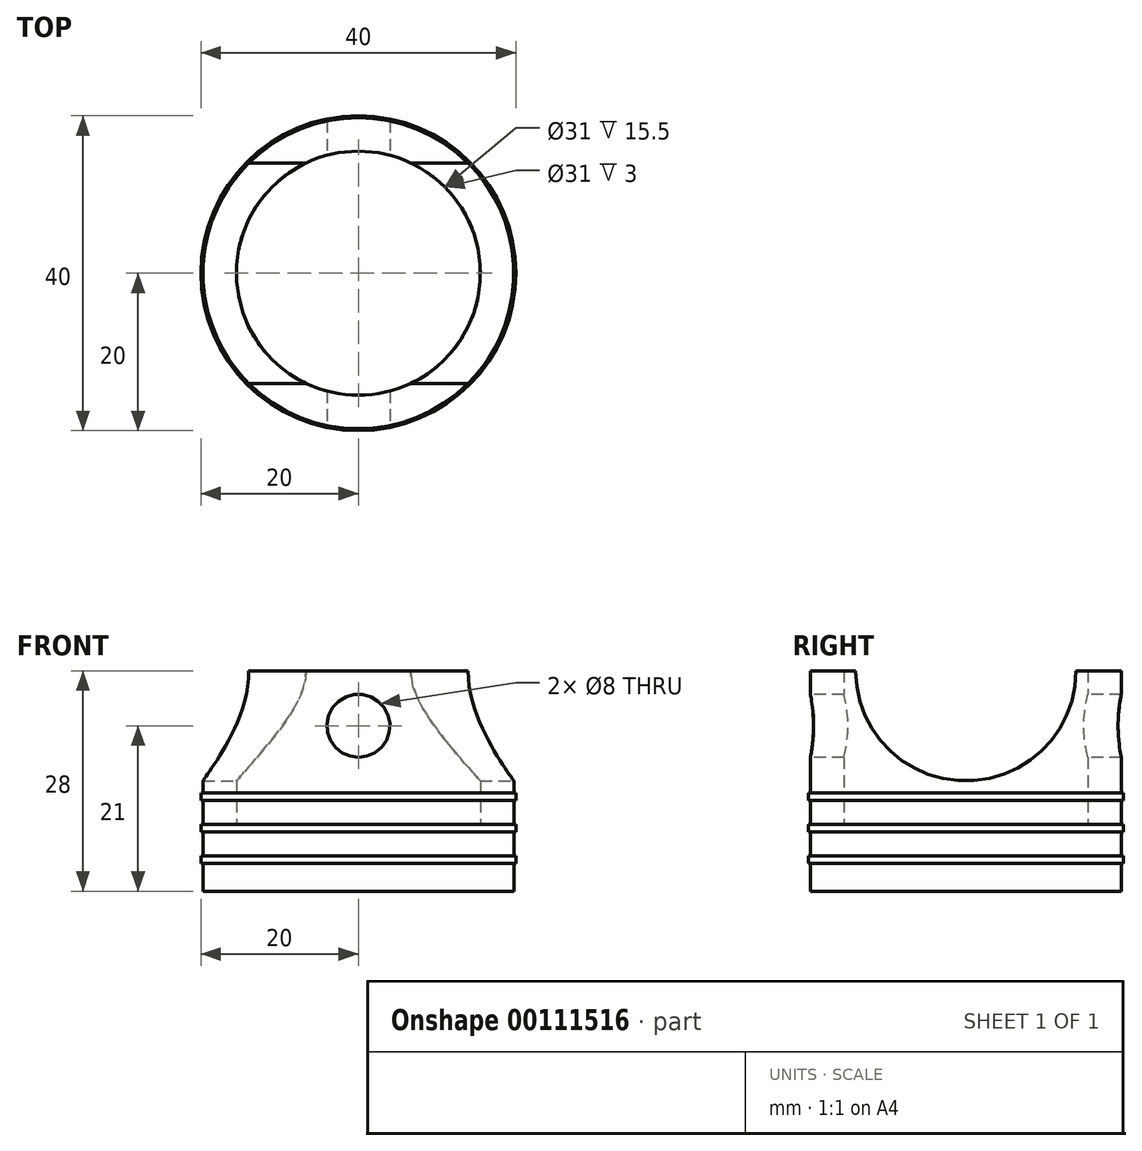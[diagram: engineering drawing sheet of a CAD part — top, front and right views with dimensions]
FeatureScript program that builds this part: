
annotation { "Feature Type Name" : "Feature", "Feature Type Description" : "" }
export const myFeature = defineFeature(function(context is Context, id is Id, definition is map)
    precondition{}
    {
        {
            var Q0;
            Q0=qCreatedBy(makeId("Top.planeOp"),FACE);
            var sketch = newSketch(context, id + "F0", { "sketchPlane" : qUnion([Q0])});
            skCircle(sketch, "E0", {"center": v(0, 0) * mm, "radius": 19.75 * mm});
            skCircle(sketch, "E1", {"center": v(0, 0) * mm, "radius": 15.5 * mm});
            skSolve(sketch);
        }
        {
            var Q0;
            Q0=makeQuery(id+"F0.imprint","IMPRINT",FACE,{"disambiguationData":[TD([[makeQuery(id+"F0.imprint","IMPRINT",EDGE,{"derivedFrom":sQuery(id+"F0.wireOp",EDGE,"E0")}),1.0]])]});
            extrude(context, id + "F1", {"entities" : qUnion([Q0]), "depth" : 28 * mm});
        }
        {
            var Q0;
            Q0=makeQuery(id+"F0.imprint","IMPRINT",FACE,{"disambiguationData":[TD([[makeQuery(id+"F0.imprint","IMPRINT",EDGE,{"derivedFrom":sQuery(id+"F0.wireOp",EDGE,"E1")}),1.0]])]});
            extrude(context, id + "F2", {"entities" : qUnion([Q0]), "operationType" : NewBodyOperationType.ADD, "depth" : 8 * mm});
        }
        {
            var Q0;
            Q0=qCreatedBy(makeId("Front.planeOp"),FACE);
            var sketch = newSketch(context, id + "F3", { "sketchPlane" : qUnion([Q0])});
            skLineSegment(sketch, "E2", {"start": v(0, 0) * mm, "end": v(0, 21) * mm});
            skCircle(sketch, "E3", {"center": v(0, 21) * mm, "radius": 4 * mm});
            skLineSegment(sketch, "E4", {"start": v(0, 21) * mm, "end": v(0, 28) * mm});
            skSolve(sketch);
        }
        {
            var Q0;
            Q0 = qSketchRegion(id + "F3", true);
            extrude(context, id + "F4", {"entities" : qUnion([Q0]), "operationType" : NewBodyOperationType.REMOVE, "endBound" : BoundingType.SYMMETRIC, "oppositeDirection" : true, "depth" : 100 * mm});
        }
        {
            var Q0;
            Q0=qCreatedBy(makeId("Front.planeOp"),FACE);
            var sketch = newSketch(context, id + "F5", { "sketchPlane" : qUnion([Q0])});
            skLineSegment(sketch, "E5", {"start": v(0, 0) * mm, "end": v(0, 4) * mm});
            skLineSegment(sketch, "E6", {"start": v(0, 0) * mm, "end": v(0, 8) * mm});
            skPoint(sketch, "E6.endSnap0", {"position": v(0, 2) * mm});
            skLineSegment(sketch, "E7", {"start": v(0, 0) * mm, "end": v(0, 12) * mm});
            skSolve(sketch);
        }
        {
            var Q0;
            Q0=sQuery(id+"F5.wireOp",VERTEX,"E5.end");
            var Q1;
            Q1=qCreatedBy(makeId("Top.planeOp"),FACE);
            cPlane(context, id + "F6", {"entities" : qUnion([Q0, Q1]), "cplaneType" : CPlaneType.PLANE_POINT, "offset" : 25 * mm, "width" : 150 * mm, "height" : 150 * mm});
        }
        {
            var Q0;
            Q0=qCreatedBy(id+"F6.planeOp",FACE);
            var sketch = newSketch(context, id + "F7", { "sketchPlane" : qUnion([Q0])});
            skCircle(sketch, "E8", {"center": v(0, 0) * mm, "radius": 20 * mm});
            skSolve(sketch);
        }
        {
            var Q0;
            Q0=makeQuery(id+"F7.imprint","IMPRINT",FACE,{"disambiguationData":[TD([[makeQuery(id+"F7.imprint","IMPRINT",EDGE,{"derivedFrom":sQuery(id+"F7.wireOp",EDGE,"E8")}),1.0]])]});
            extrude(context, id + "F8", {"entities" : qUnion([Q0]), "operationType" : NewBodyOperationType.ADD, "endBound" : BoundingType.SYMMETRIC, "depth" : 1 * mm});
        }
        {
            var Q0;
            Q0=sQuery(id+"F5.wireOp",VERTEX,"E6.end");
            var Q1;
            Q1=qCreatedBy(makeId("Top.planeOp"),FACE);
            cPlane(context, id + "F9", {"entities" : qUnion([Q0, Q1]), "cplaneType" : CPlaneType.PLANE_POINT, "offset" : 25 * mm, "width" : 150 * mm, "height" : 150 * mm});
        }
        {
            var Q0;
            Q0=qCreatedBy(id+"F9.planeOp",FACE);
            var sketch = newSketch(context, id + "F10", { "sketchPlane" : qUnion([Q0])});
            skCircle(sketch, "E9", {"center": v(0, 0) * mm, "radius": 20 * mm});
            skSolve(sketch);
        }
        {
            var Q0;
            Q0=makeQuery(id+"F10.imprint","IMPRINT",FACE,{"disambiguationData":[TD([[makeQuery(id+"F10.imprint","IMPRINT",EDGE,{"derivedFrom":sQuery(id+"F10.wireOp",EDGE,"E9")}),1.0]])]});
            extrude(context, id + "F11", {"entities" : qUnion([Q0]), "operationType" : NewBodyOperationType.ADD, "endBound" : BoundingType.SYMMETRIC, "depth" : 1 * mm});
        }
        {
            var Q0;
            Q0=sQuery(id+"F5.wireOp",VERTEX,"E7.end");
            var Q1;
            Q1=qCreatedBy(makeId("Top.planeOp"),FACE);
            cPlane(context, id + "F12", {"entities" : qUnion([Q0, Q1]), "cplaneType" : CPlaneType.PLANE_POINT, "offset" : 25 * mm, "width" : 150 * mm, "height" : 150 * mm});
        }
        {
            var Q0;
            Q0=qCreatedBy(id+"F12.planeOp",FACE);
            var sketch = newSketch(context, id + "F13", { "sketchPlane" : qUnion([Q0])});
            skCircle(sketch, "E10", {"center": v(0, 0) * mm, "radius": 20 * mm});
            skSolve(sketch);
        }
        {
            var Q0;
            Q0=makeQuery(id+"F13.imprint","IMPRINT",FACE,{"disambiguationData":[TD([[makeQuery(id+"F13.imprint","IMPRINT",EDGE,{"derivedFrom":sQuery(id+"F13.wireOp",EDGE,"E10")}),1.0]])]});
            extrude(context, id + "F14", {"entities" : qUnion([Q0]), "operationType" : NewBodyOperationType.ADD, "endBound" : BoundingType.SYMMETRIC, "depth" : 1 * mm});
        }
        {
            var Q0;
            Q0=qCreatedBy(makeId("Right.planeOp"),FACE);
            var sketch = newSketch(context, id + "F15", { "sketchPlane" : qUnion([Q0])});
            skLineSegment(sketch, "E11", {"start": v(0, 0) * mm, "end": v(0, 28) * mm});
            skCircle(sketch, "E12", {"center": v(0, 28) * mm, "radius": 14 * mm});
            skLineSegment(sketch, "E13", {"start": v(0, 28) * mm, "end": v(14, 28) * mm});
            skLineSegment(sketch, "E14", {"start": v(14, 28) * mm, "end": v(-14, 28) * mm});
            skSolve(sketch);
        }
        {
            var Q0;
            {var subQ0=sQuery(id+"F15.wireOp",EDGE,"E14");var subQ1=sQuery(id+"F15.wireOp",EDGE,"E11");var subQ2=makeQuery(id+"F15.imprint","INTERSECT",VERTEX,{"derivedFrom":[subQ1,subQ0]});Q0=makeQuery(id+"F15.imprint","IMPRINT",FACE,{"disambiguationData":[TD([[makeQuery(id+"F15.imprint","IMPRINT",EDGE,{"disambiguationData":[TD([[subQ2,1.0]])],"derivedFrom":subQ1}),1.0]])]});}
            var Q1;
            {var subQ0=sQuery(id+"F15.wireOp",EDGE,"E14");var subQ1=sQuery(id+"F15.wireOp",EDGE,"E11");var subQ2=makeQuery(id+"F15.imprint","INTERSECT",VERTEX,{"derivedFrom":[subQ1,subQ0]});Q1=makeQuery(id+"F15.imprint","IMPRINT",FACE,{"disambiguationData":[TD([[makeQuery(id+"F15.imprint","IMPRINT",EDGE,{"disambiguationData":[TD([[subQ2,1.0]])],"derivedFrom":subQ1}),-1.0]])]});}
            extrude(context, id + "F16", {"entities" : qUnion([Q0, Q1]), "operationType" : NewBodyOperationType.REMOVE, "endBound" : BoundingType.SYMMETRIC, "oppositeDirection" : true, "depth" : 100 * mm});
        }
    });
